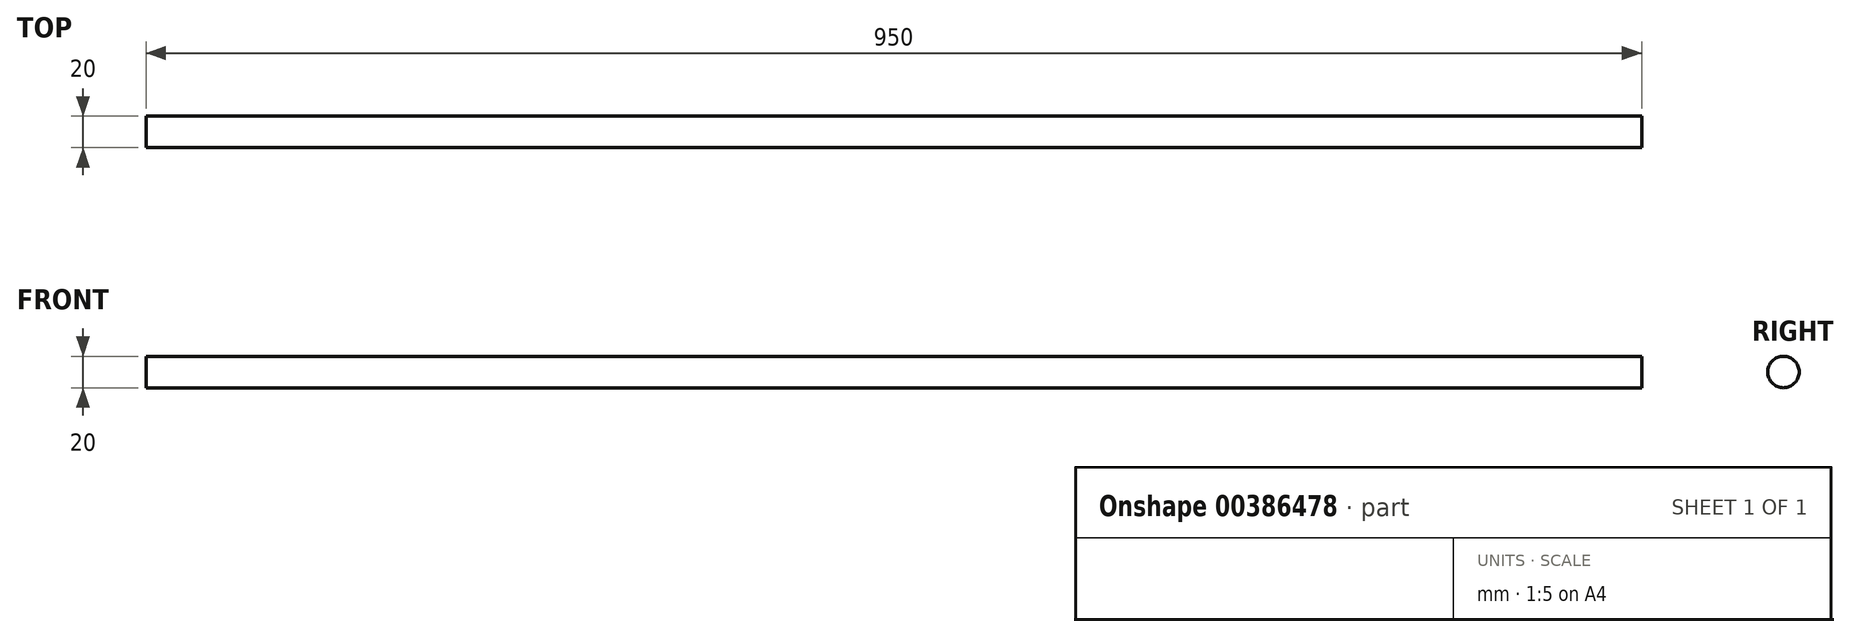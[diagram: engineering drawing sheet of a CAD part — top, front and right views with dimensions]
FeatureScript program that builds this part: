
annotation { "Feature Type Name" : "Feature", "Feature Type Description" : "" }
export const myFeature = defineFeature(function(context is Context, id is Id, definition is map)
    precondition{}
    {
        {
            var Q0;
            Q0=qCreatedBy(makeId("Right.planeOp"),FACE);
            var sketch = newSketch(context, id + "F0", { "sketchPlane" : qUnion([Q0])});
            skCircle(sketch, "E0", {"center": v(0, 0) * mm, "radius": 10 * mm});
            skSolve(sketch);
        }
        {
            var Q0;
            Q0=makeQuery(id+"F0.imprint","IMPRINT",FACE,{"disambiguationData":[TD([[makeQuery(id+"F0.imprint","IMPRINT",EDGE,{"derivedFrom":sQuery(id+"F0.wireOp",EDGE,"E0")}),1.0]])]});
            extrude(context, id + "F1", {"entities" : qUnion([Q0]), "depth" : 950 * mm});
        }
    });
